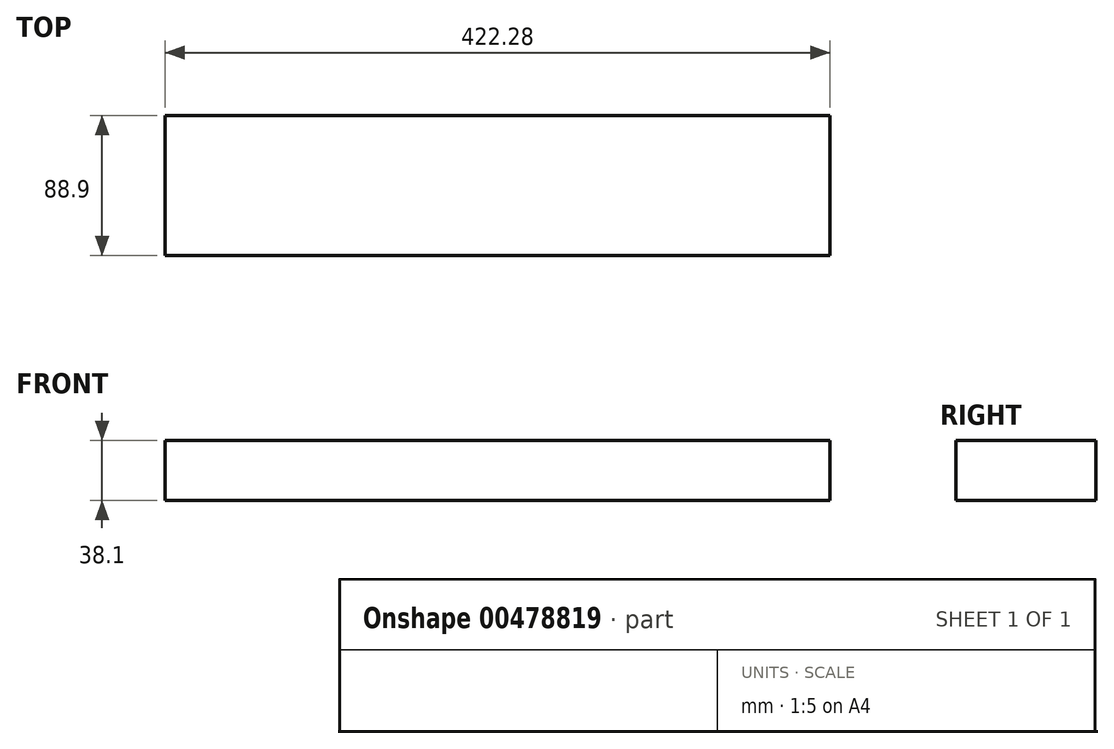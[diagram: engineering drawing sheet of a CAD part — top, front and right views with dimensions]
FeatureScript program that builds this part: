
annotation { "Feature Type Name" : "Feature", "Feature Type Description" : "" }
export const myFeature = defineFeature(function(context is Context, id is Id, definition is map)
    precondition{}
    {
        {
            var Q0;
            Q0=qCreatedBy(makeId("Front.planeOp"),FACE);
            var sketch = newSketch(context, id + "F0", { "sketchPlane" : qUnion([Q0])});
            skLineSegment(sketch, "E0.bottom", {"start": v(0, 0) * mm, "end": v(422.28, 0) * mm});
            skLineSegment(sketch, "E0.top", {"start": v(0, 38.1) * mm, "end": v(422.28, 38.1) * mm});
            skLineSegment(sketch, "E0.left", {"start": v(0, 0) * mm, "end": v(0, 38.1) * mm});
            skLineSegment(sketch, "E0.right", {"start": v(422.28, 0) * mm, "end": v(422.28, 38.1) * mm});
            skSolve(sketch);
        }
        {
            var Q0;
            Q0 = qSketchRegion(id + "F0", true);
            extrude(context, id + "F1", {"entities" : qUnion([Q0]), "depth" : 88.9 * mm});
        }
    });
